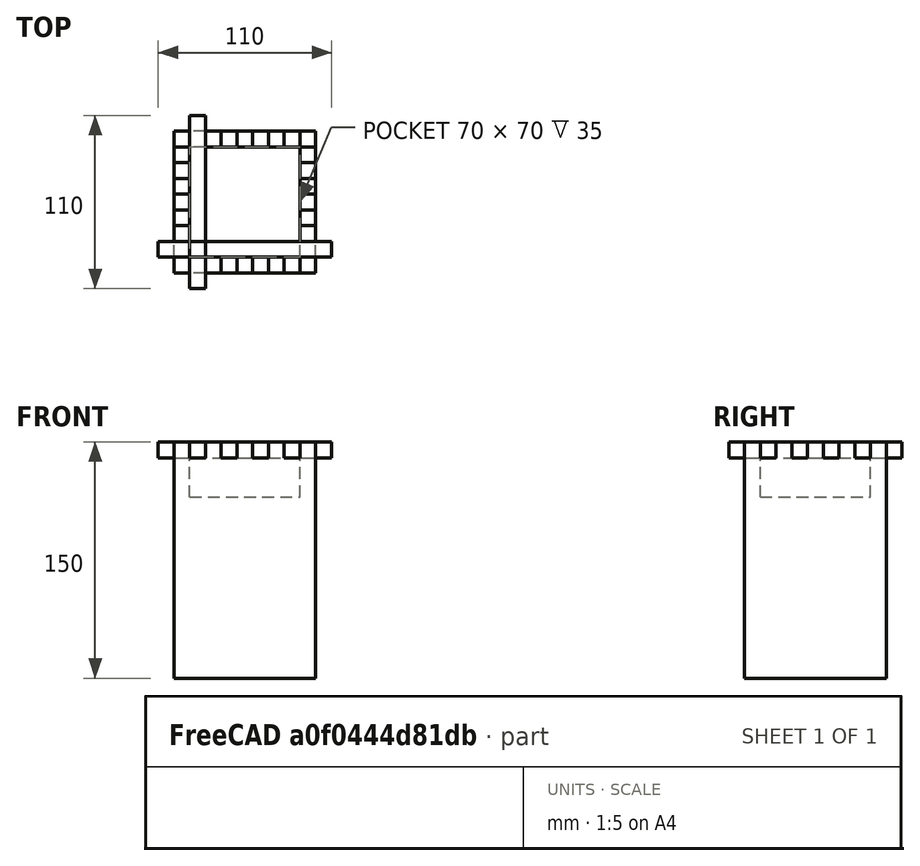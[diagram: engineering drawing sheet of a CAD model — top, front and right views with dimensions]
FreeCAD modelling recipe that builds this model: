
FCSTD DOCUMENT  (FreeCAD 0.21R33771 (Git))
Label: OJT1_T10R02_torre
License: All rights reserved
LicenseURL: http://en.wikipedia.org/wiki/All_rights_reserved
objects: Part::Box×4, Part::MultiFuse×3, Part::Cut×2, Part::FeaturePython×2
note: 9 computed .brp shape members not serialized (recipe doc carries the construction recipe); baked Part::Feature solids carry a one-line shape summary decoded from their .brp

FEATURE [Part::Box] Box  label="Cube"
  AttacherType = Attacher::AttachEngine3D
  Height = 150
  Length = 90
  Width = 90
FEATURE [Part::Box] Box001  label="Cube001"
  AttacherType = Attacher::AttachEngine3D
  Height = 70
  Length = 70
  Placement = pos=(10,10,115) rot=(0,0,1;0rad)
  Width = 70
FEATURE [Part::Cut] Cut
  Base = -> Box
  Refine = true
  Tool = -> Box001
FEATURE [Part::Box] Box002  label="Cube002"
  AttacherType = Attacher::AttachEngine3D
  Height = 10
  Length = 110
  Placement = pos=(-10,10,140) rot=(0,0,1;0rad)
  Width = 10
FEATURE [Part::FeaturePython] Array  # Draft array (typed FeaturePython)
  AlwaysSyncPlacement = false
  Angle = 360
  ArrayType = 0
  Axis = (0,0,1)
  Base = -> Box002
  Center = (0,0,0)
  Count = 4
  ExpandArray = false
  Fuse = false
  IntervalAxis = (0,0,0)
  IntervalX = (0,20,0)
  IntervalY = (0,20,0)
  IntervalZ = (0,0,0)
  NumberCircles = 3
  NumberPolar = 5
  NumberX = 4
  NumberY = 1
  NumberZ = 1
  PlacementList = 4 placements: arithmetic series from (-10,10,140) step (0,20,0) to (-10,70,140)
  RadialDistance = 50
  ScaleList = (4) [(1,1,1),(1,1,1),(1,1,1),(1,1,1)]
  Symmetry = 1
  TangentialDistance = 25
FEATURE [Part::Box] Box003  label="Cube003"
  AttacherType = Attacher::AttachEngine3D
  Height = 10
  Length = 10
  Placement = pos=(10,-10,140) rot=(0,0,1;0rad)
  Width = 110
FEATURE [Part::FeaturePython] Array001  # Draft array (typed FeaturePython)
  AlwaysSyncPlacement = false
  Angle = 360
  ArrayType = 0
  Axis = (0,0,1)
  Base = -> Box003
  Center = (0,0,0)
  Count = 4
  ExpandArray = false
  Fuse = false
  IntervalAxis = (0,0,0)
  IntervalX = (20,0,0)
  IntervalY = (0,0,0)
  IntervalZ = (0,0,0)
  NumberCircles = 3
  NumberPolar = 5
  NumberX = 4
  NumberY = 1
  NumberZ = 1
  PlacementList = 4 placements: arithmetic series from (10,-10,140) step (20,0,0) to (70,-10,140)
  RadialDistance = 50
  ScaleList = (4) [(1,1,1),(1,1,1),(1,1,1),(1,1,1)]
  Symmetry = 1
  TangentialDistance = 25
FEATURE [Part::MultiFuse] Fusion
  Refine = true
  Shapes = -> [Array]
FEATURE [Part::MultiFuse] Fusion001
  Refine = true
  Shapes = -> [Array001]
FEATURE [Part::MultiFuse] Fusion002
  Refine = true
  Shapes = -> [Fusion,Fusion001]
FEATURE [Part::Cut] Cut001  label="torre"
  Base = -> Cut
  Refine = true
  Tool = -> Fusion002
